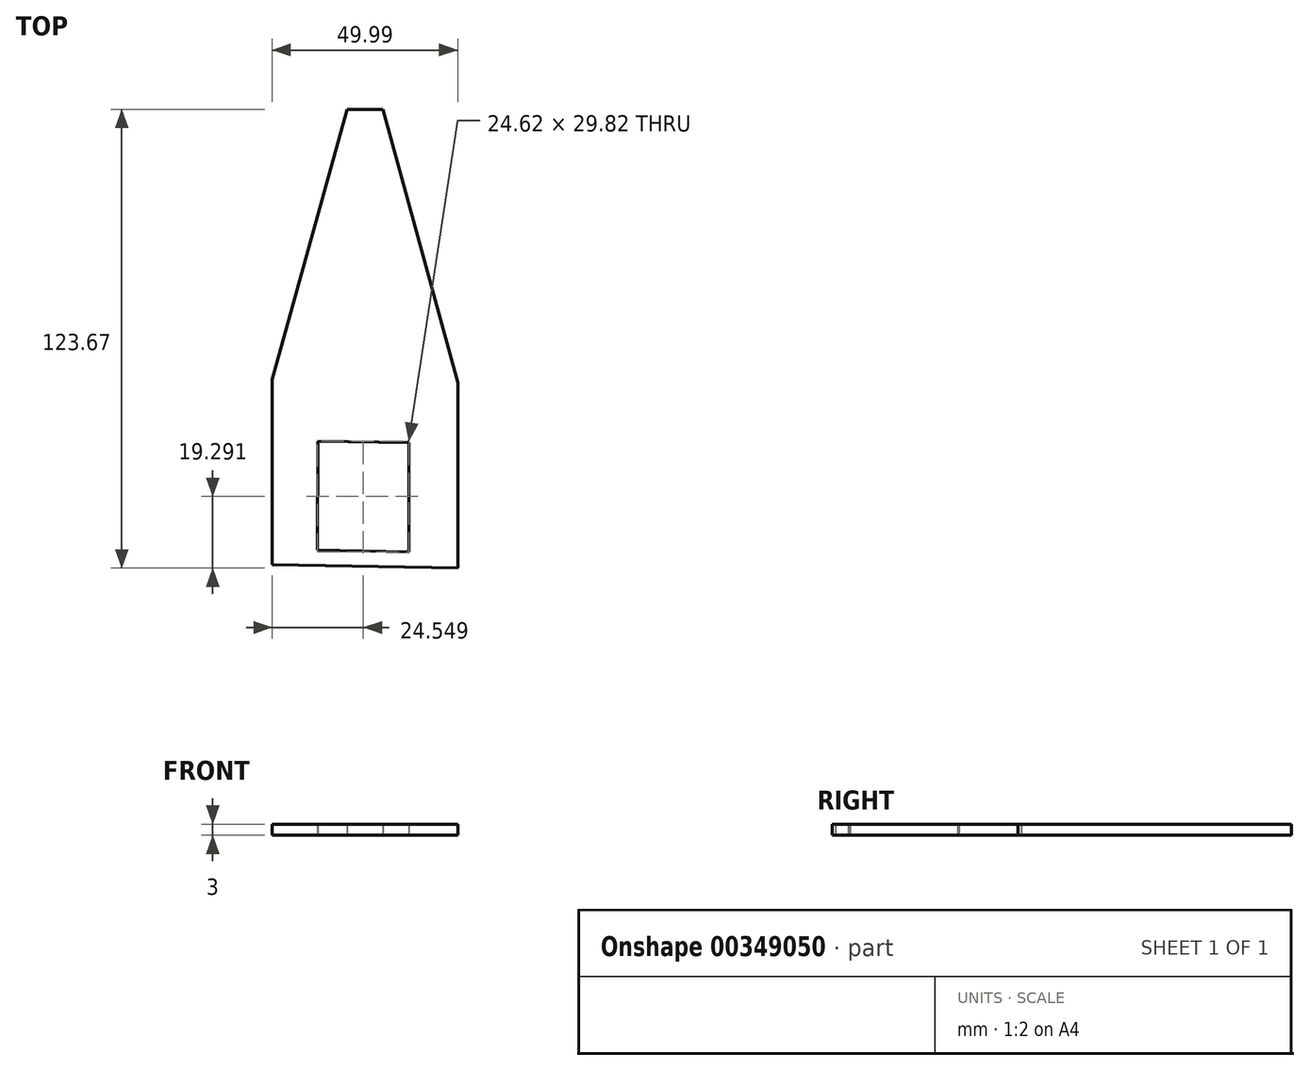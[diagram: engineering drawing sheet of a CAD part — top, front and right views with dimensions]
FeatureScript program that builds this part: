
annotation { "Feature Type Name" : "Feature", "Feature Type Description" : "" }
export const myFeature = defineFeature(function(context is Context, id is Id, definition is map)
    precondition{}
    {
        {
            var Q0;
            Q0=qCreatedBy(makeId("Top.planeOp"),FACE);
            var sketch = newSketch(context, id + "F0", { "sketchPlane" : qUnion([Q0])});
            skLineSegment(sketch, "E0", {"start": v(3.55, -72.72) * mm, "end": v(3.55, -22.72) * mm});
            skLineSegment(sketch, "E1", {"start": v(3.55, -22.72) * mm, "end": v(23.72, 50.08) * mm});
            skLineSegment(sketch, "E2", {"start": v(23.72, 50.08) * mm, "end": v(33.37, 50.08) * mm});
            skLineSegment(sketch, "E3", {"start": v(33.37, 50.08) * mm, "end": v(53.54, -23.6) * mm});
            skLineSegment(sketch, "E4", {"start": v(53.54, -23.6) * mm, "end": v(53.54, -73.6) * mm});
            skLineSegment(sketch, "E5", {"start": v(53.54, -73.6) * mm, "end": v(3.55, -72.72) * mm});
            skLineSegment(sketch, "E6", {"start": v(15.83, -39.39) * mm, "end": v(40.4, -39.82) * mm});
            skLineSegment(sketch, "E7", {"start": v(40.4, -39.82) * mm, "end": v(40.4, -69.2) * mm});
            skLineSegment(sketch, "E8", {"start": v(40.4, -69.2) * mm, "end": v(15.79, -68.78) * mm});
            skLineSegment(sketch, "E9", {"start": v(15.79, -68.78) * mm, "end": v(15.83, -39.39) * mm});
            skLineSegment(sketch, "E10", {"start": v(-48.09, -7.18) * mm, "end": v(-37.8, -7.18) * mm});
            skLineSegment(sketch, "E11", {"start": v(-37.8, -7.18) * mm, "end": v(-37.8, -17.42) * mm});
            skLineSegment(sketch, "E12", {"start": v(-37.8, -17.42) * mm, "end": v(-48.09, -17.42) * mm});
            skLineSegment(sketch, "E13", {"start": v(-48.09, -17.42) * mm, "end": v(-48.09, -7.18) * mm});
            skLineSegment(sketch, "E14", {"start": v(-46.35, -8) * mm, "end": v(-39.46, -8) * mm});
            skLineSegment(sketch, "E15", {"start": v(-39.46, -8) * mm, "end": v(-38.68, -8.78) * mm});
            skLineSegment(sketch, "E16", {"start": v(-38.68, -8.78) * mm, "end": v(-38.68, -15.66) * mm});
            skLineSegment(sketch, "E17", {"start": v(-38.68, -15.66) * mm, "end": v(-39.5, -16.6) * mm});
            skLineSegment(sketch, "E18", {"start": v(-39.5, -16.6) * mm, "end": v(-46.38, -16.6) * mm});
            skLineSegment(sketch, "E19", {"start": v(-46.38, -16.6) * mm, "end": v(-47.25, -15.62) * mm});
            skLineSegment(sketch, "E20", {"start": v(-47.25, -15.62) * mm, "end": v(-47.25, -8.97) * mm});
            skLineSegment(sketch, "E21", {"start": v(-47.25, -8.97) * mm, "end": v(-46.35, -8) * mm});
            skLineSegment(sketch, "E22", {"start": v(-68.94, -6.26) * mm, "end": v(-57.37, -6.26) * mm});
            skLineSegment(sketch, "E23", {"start": v(-57.37, -6.26) * mm, "end": v(-57.37, -18.03) * mm});
            skLineSegment(sketch, "E24", {"start": v(-57.37, -18.03) * mm, "end": v(-68.94, -18.03) * mm});
            skLineSegment(sketch, "E25", {"start": v(-68.94, -18.03) * mm, "end": v(-68.94, -6.26) * mm});
            skSolve(sketch);
        }
        {
            var Q0;
            Q0=makeQuery(id+"F0.imprint","IMPRINT",FACE,{"disambiguationData":[TD([[makeQuery(id+"F0.imprint","IMPRINT",EDGE,{"derivedFrom":sQuery(id+"F0.wireOp",EDGE,"E0")}),-1.0]])]});
            extrude(context, id + "F1", {"entities" : qUnion([Q0]), "depth" : 3 * mm});
        }
    });
